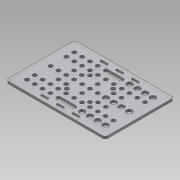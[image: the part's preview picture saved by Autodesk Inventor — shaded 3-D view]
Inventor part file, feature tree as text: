
AUTODESK INVENTOR PART (.ipt)
format: ipt  version: 2013 SP2 (Build 170200200, 200)  size: 303,616 bytes
history: native  units: mm
features: sketch x7, hole x4, extrude x3, mirror x2, fillet x1, plane x1
ambient origin geometry x8: Origin, YZ Plane, XZ Plane, XY Plane, X Axis, Y Axis, Z Axis, Center Point
bodies: Solid1 (feature_tree)
feature tree (18):
  extrude  "Extrusion1"  Depth=88.0mm
  fillet  "Fillet1"  [1 undecoded]
  hole  "Hole2"  [1 undecoded]
  hole  "Hole3"  [1 undecoded]
  extrude  "Extrusion2"  Depth=74.32mm
  plane  "Work Plane1"
  mirror  "Mirror1"
  extrude  "Extrusion3"  Depth=20.32mm
  mirror  "Mirror2"
  hole  "Hole4"  [1 undecoded]
  hole  "Hole5"  [1 undecoded]
  sketch  "Sketch1"  dims[d0=127.0mm d1=88.0mm d3=0.0mm]
  sketch  "Sketch4"  dims[d18=50.0mm d20=10.0mm d36=3.36mm d37=13.68mm]
  sketch  "Sketch5"  dims[d38=23.68mm d39=44.0mm]
  sketch  "Sketch6"  dims[d40=64.32mm d41=74.32mm]
  sketch  "Sketch7"  dims[d42=10.16mm d43=20.32mm]
  sketch  "Sketch8"  dims[d44=40.0mm d46=10.0mm d47=10.0mm d49=10.0mm]
  sketch  "Sketch9"  dims[d52=40.0mm d54=10.0mm d55=10.16mm d56=20.32mm d57=10.0mm d59=40.0mm d61=10.0mm d62=20.32mm d63=10.0mm d64=10.0mm d65=5.0mm d66=6.0mm d67=4.0mm d68=2.0mm d69=90.0deg d70=8.0mm d71=20.594885mm d72=7.14mm d73=6.0mm d74=4.0mm d75=2.0mm d76=90.0deg d77=8.0mm d78=20.594885mm d79=5.98mm d82=6.98mm d83=2.5mm d84=9.5mm d85=20.0mm d87=20.0mm d88=20.0mm d90=20.0mm d93=10.0mm d94=0.0mm d95=25.0mm d96=13.68mm d97=20.0mm d98=2.5mm d99=2.5mm d100=1.973956mm d101=1.973956mm d102=51.0mm d103=51.0mm d104=53.5mm d105=76.0mm d106=10.0mm d107=0.0mm d108=34.0mm d109=10.0mm d110=5.0mm d111=6.0mm d112=4.0mm d113=2.0mm d114=90.0deg d115=8.0mm d116=20.594885mm d117=14.82mm d118=14.825mm d119=5.0mm d120=6.0mm d121=4.0mm d122=2.0mm d123=90.0deg d124=8.0mm d125=20.594885mm]
note: 5 required parameter values undecoded (feature->parameter linkage not recoverable at this tier; creation-order binding heuristic only, values carry confidence <= 0.55)
